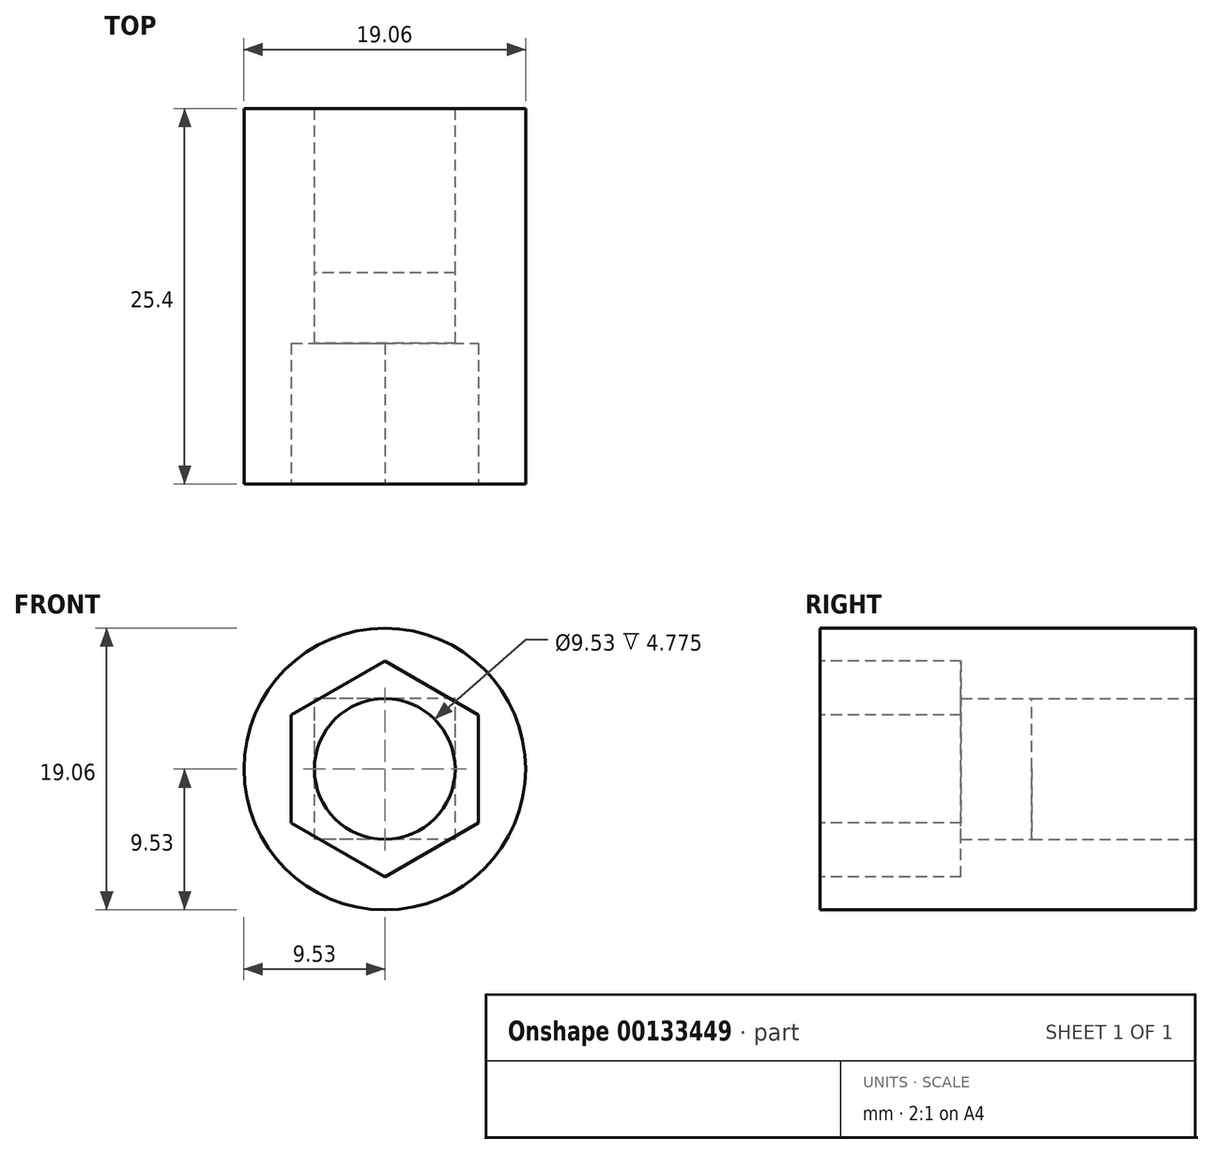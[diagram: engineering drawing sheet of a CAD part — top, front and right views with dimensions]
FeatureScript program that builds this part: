
annotation { "Feature Type Name" : "Feature", "Feature Type Description" : "" }
export const myFeature = defineFeature(function(context is Context, id is Id, definition is map)
    precondition{}
    {
        {
            var Q0;
            Q0=qCreatedBy(makeId("Front.planeOp"),FACE);
            var sketch = newSketch(context, id + "F0", { "sketchPlane" : qUnion([Q0])});
            skCircle(sketch, "E0", {"center": v(0, 0) * mm, "radius": 9.53 * mm});
            skSolve(sketch);
        }
        {
            var Q0;
            Q0 = qSketchRegion(id + "F0", true);
            extrude(context, id + "F1", {"entities" : qUnion([Q0]), "depth" : 25.4 * mm});
        }
        {
            var Q0;
            Q0=qCreatedBy(makeId("Front.planeOp"),FACE);
            var sketch = newSketch(context, id + "F2", { "sketchPlane" : qUnion([Q0])});
            skLineSegment(sketch, "E1.bottom", {"start": v(4.76, -4.76) * mm, "end": v(-4.76, -4.76) * mm});
            skLineSegment(sketch, "E1.top", {"start": v(4.76, 4.76) * mm, "end": v(-4.76, 4.76) * mm});
            skLineSegment(sketch, "E1.left", {"start": v(4.76, -4.76) * mm, "end": v(4.76, 4.76) * mm});
            skLineSegment(sketch, "E1.right", {"start": v(-4.76, -4.76) * mm, "end": v(-4.76, 4.76) * mm});
            skPoint(sketch, "E1.middle", {"position": v(0, 0) * mm});
            skCircle(sketch, "E2", {"center": v(0, 0) * mm, "radius": 4.76 * mm});
            skSolve(sketch);
        }
        {
            var Q0;
            {var subQ0=sQuery(id+"F2.wireOp",EDGE,"E2");var subQ1=makeQuery(id+"F2.imprint","INTERSECT",VERTEX,{"derivedFrom":[sQuery(id+"F2.wireOp",EDGE,"E1.top"),subQ0]});Q0=makeQuery(id+"F2.imprint","IMPRINT",FACE,{"disambiguationData":[TD([[makeQuery(id+"F2.imprint","IMPRINT",EDGE,{"disambiguationData":[TD([[subQ1,1.0]])],"derivedFrom":subQ0}),1.0]])]});}
            extrude(context, id + "F3", {"entities" : qUnion([Q0]), "operationType" : NewBodyOperationType.REMOVE, "endBound" : BoundingType.THROUGH_ALL, "depth" : 25.4 * mm});
        }
        {
            var Q0;
            Q0 = qSketchRegion(id + "F2", true);
            extrude(context, id + "F4", {"entities" : qUnion([Q0]), "operationType" : NewBodyOperationType.REMOVE, "depth" : 11.1 * mm});
        }
        {
            var Q0;
            Q0=makeQuery(id+"F1.opExtrude","CAP_FACE",FACE,{"disambiguationData":[OSD([sQuery(id+"F0.wireOp",EDGE,"E0")])],"isStart":false});
            var sketch = newSketch(context, id + "F5", { "sketchPlane" : qUnion([Q0])});
            skCircle(sketch, "E3.cCircle", {"center": v(0, 0) * mm, "radius": 6.32 * mm, "construction": true});
            skLineSegment(sketch, "E3.0", {"start": v(6.32, 3.65) * mm, "end": v(6.32, -3.65) * mm});
            skLineSegment(sketch, "E3.1", {"start": v(6.32, -3.65) * mm, "end": v(0, -7.3) * mm});
            skLineSegment(sketch, "E3.2", {"start": v(0, -7.3) * mm, "end": v(-6.32, -3.65) * mm});
            skLineSegment(sketch, "E3.3", {"start": v(-6.32, -3.65) * mm, "end": v(-6.32, 3.65) * mm});
            skLineSegment(sketch, "E3.4", {"start": v(-6.32, 3.65) * mm, "end": v(0, 7.3) * mm});
            skLineSegment(sketch, "E3.5", {"start": v(0, 7.3) * mm, "end": v(6.32, 3.65) * mm});
            skPoint(sketch, "E3.0.midPoint", {"position": v(6.32, 0) * mm});
            skSolve(sketch);
        }
        {
            var Q0;
            Q0 = qSketchRegion(id + "F5", true);
            extrude(context, id + "F6", {"entities" : qUnion([Q0]), "operationType" : NewBodyOperationType.REMOVE, "oppositeDirection" : true, "depth" : 9.52 * mm});
        }
    });
